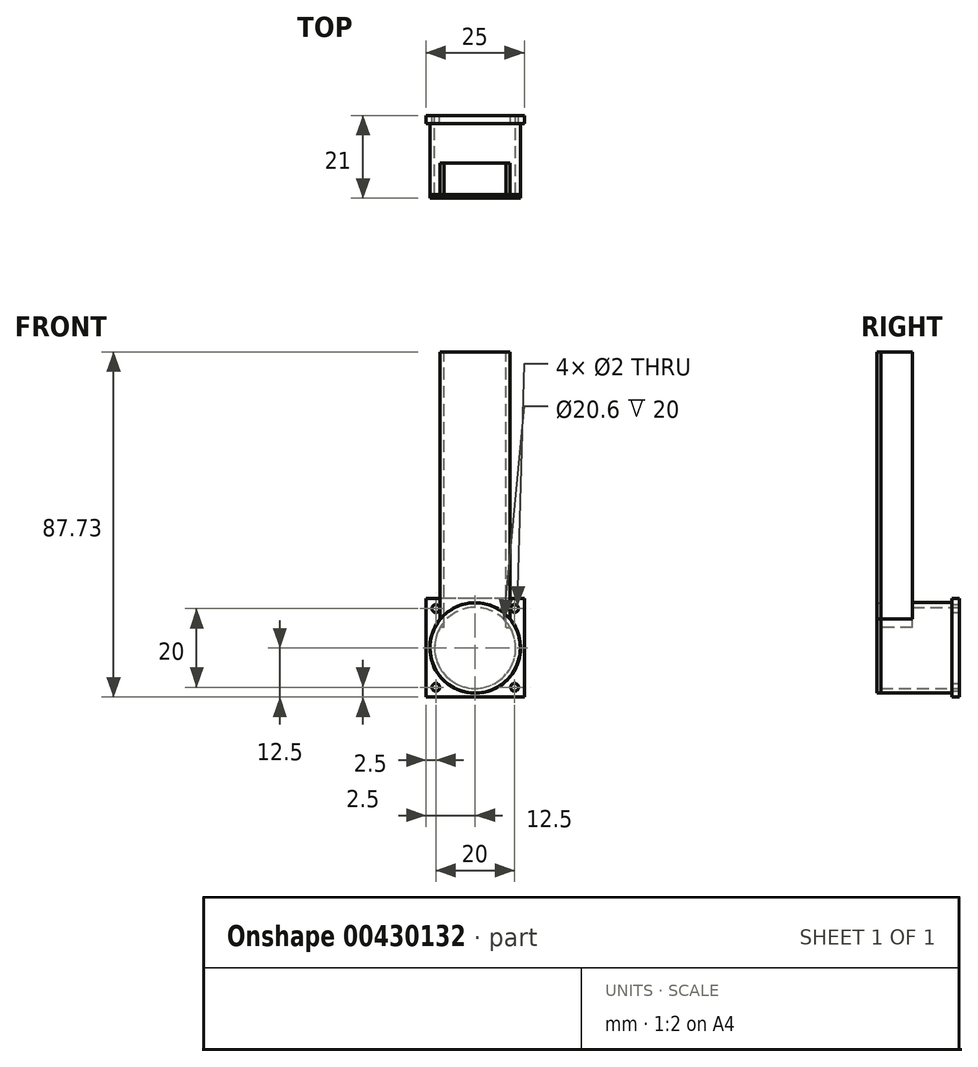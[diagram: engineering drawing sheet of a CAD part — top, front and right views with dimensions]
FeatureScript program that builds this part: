
annotation { "Feature Type Name" : "Feature", "Feature Type Description" : "" }
export const myFeature = defineFeature(function(context is Context, id is Id, definition is map)
    precondition{}
    {
        {
            var Q0;
            Q0=qCreatedBy(makeId("Front.planeOp"),FACE);
            var sketch = newSketch(context, id + "F0", { "sketchPlane" : qUnion([Q0])});
            skLineSegment(sketch, "E0.bottom", {"start": v(12.5, 12.5) * mm, "end": v(-12.5, 12.5) * mm});
            skLineSegment(sketch, "E0.top", {"start": v(12.5, -12.5) * mm, "end": v(-12.5, -12.5) * mm});
            skLineSegment(sketch, "E0.left", {"start": v(12.5, 12.5) * mm, "end": v(12.5, -12.5) * mm});
            skLineSegment(sketch, "E0.right", {"start": v(-12.5, 12.5) * mm, "end": v(-12.5, -12.5) * mm});
            skPoint(sketch, "E0.middle", {"position": v(0, 0) * mm});
            skCircle(sketch, "E1", {"center": v(0, 0) * mm, "radius": 11.5 * mm});
            skCircle(sketch, "E2.0", {"center": v(0, 0) * mm, "radius": 10.3 * mm});
            skCircle(sketch, "E3", {"center": v(-10, 10) * mm, "radius": 1 * mm});
            skLineSegment(sketch, "E4", {"start": v(0, -14.34) * mm, "end": v(0, 50.34) * mm, "construction": true});
            skLineSegment(sketch, "E5", {"start": v(-25.01, 0) * mm, "end": v(43.33, 0) * mm, "construction": true});
            skCircle(sketch, "E6.MirrorC", {"center": v(10, 10) * mm, "radius": 1 * mm});
            skCircle(sketch, "E7.MirrorC", {"center": v(-10, -10) * mm, "radius": 1 * mm});
            skCircle(sketch, "E8.MirrorC", {"center": v(10, -10) * mm, "radius": 1 * mm});
            skLineSegment(sketch, "E9", {"start": v(0, 50.34) * mm, "end": v(0, 167.06) * mm, "construction": true});
            skSolve(sketch);
        }
        {
            var Q0;
            Q0=makeQuery(id+"F0.imprint","IMPRINT",FACE,{"disambiguationData":[TD([[makeQuery(id+"F0.imprint","IMPRINT",EDGE,{"derivedFrom":sQuery(id+"F0.wireOp",EDGE,"E1")}),1.0]])]});
            extrude(context, id + "F1", {"entities" : qUnion([Q0]), "depth" : 20 * mm});
        }
        {
            var Q0;
            Q0 = qSketchRegion(id + "F0", true);
            extrude(context, id + "F2", {"entities" : qUnion([Q0]), "operationType" : NewBodyOperationType.ADD, "depth" : 2 * mm});
        }
        {
            var Q0;
            Q0=makeQuery(id+"F1.opExtrude","CAP_FACE",FACE,{"disambiguationData":[OSD([sQuery(id+"F0.wireOp",EDGE,"E1"),sQuery(id+"F0.wireOp",EDGE,"E2.0")])],"isStart":false});
            var sketch = newSketch(context, id + "F3", { "sketchPlane" : qUnion([Q0])});
            skLineSegment(sketch, "E10", {"start": v(-8.88, 7.31) * mm, "end": v(-8.88, 5.23) * mm});
            skLineSegment(sketch, "E11.MirrorCS", {"start": v(8.88, 7.31) * mm, "end": v(8.88, 5.23) * mm});
            skLineSegment(sketch, "E12", {"start": v(0, 14.57) * mm, "end": v(0, -15.36) * mm, "construction": true});
            skSolve(sketch);
        }
        {
            var Q0;
            Q0 = qSketchRegion(id + "F3", true);
            var Q1;
            {var subQ0=sQuery(id+"F3.wireOp",EDGE,"E10");Q1=makeQuery(id+"F3.imprint","IMPRINT",FACE,{"disambiguationData":[TD([[makeQuery(id+"F3.imprint","IMPRINT",EDGE,{"derivedFrom":subQ0}),1.0]])]});}
            extrude(context, id + "F4", {"entities" : qUnion([Q0, Q1]), "operationType" : NewBodyOperationType.REMOVE, "oppositeDirection" : true, "depth" : 8 * mm});
        }
        {
            var Q0;
            Q0=makeQuery(id+"F1.opExtrude","CAP_FACE",FACE,{"disambiguationData":[OSD([sQuery(id+"F0.wireOp",EDGE,"E1"),sQuery(id+"F0.wireOp",EDGE,"E2.0")])],"isStart":false});
            var sketch = newSketch(context, id + "F5", { "sketchPlane" : qUnion([Q0])});
            skCircle(sketch, "E13", {"center": v(0, 0) * mm, "radius": 11.46 * mm});
            skSolve(sketch);
        }
        {
            var Q0;
            Q0 = qSketchRegion(id + "F5", true);
            extrude(context, id + "F6", {"entities" : qUnion([Q0]), "operationType" : NewBodyOperationType.ADD, "depth" : 1 * mm});
        }
        {
            var Q0;
            Q0=makeQuery(id+"F4.boolean.opBoolean","COPY",FACE,{"derivedFrom":makeQuery(id+"F4.opExtrude","SWEPT_FACE",FACE,{"disambiguationData":[OSD([sQuery(id+"F3.wireOp",EDGE,"E10")])]})});
            var sketch = newSketch(context, id + "F7", { "sketchPlane" : qUnion([Q0])});
            skLineSegment(sketch, "E14", {"start": v(-20, 5.23) * mm, "end": v(-20, 75.23) * mm});
            skLineSegment(sketch, "E15", {"start": v(-12, 5.23) * mm, "end": v(-12, 75.23) * mm});
            skLineSegment(sketch, "E16", {"start": v(-20, 75.23) * mm, "end": v(-12, 75.23) * mm});
            skLineSegment(sketch, "E17", {"start": v(-12, 5.23) * mm, "end": v(-20, 5.23) * mm});
            skSolve(sketch);
        }
        {
            var Q0;
            Q0=makeQuery(id+"F4.boolean.opBoolean","COPY",FACE,{"derivedFrom":makeQuery(id+"F4.opExtrude","SWEPT_FACE",FACE,{"disambiguationData":[OSD([sQuery(id+"F3.wireOp",EDGE,"E11.MirrorCS")])]})});
            var sketch = newSketch(context, id + "F8", { "sketchPlane" : qUnion([Q0])});
            skLineSegment(sketch, "E18", {"start": v(20, 5.23) * mm, "end": v(20, 75.23) * mm});
            skLineSegment(sketch, "E19", {"start": v(12, 5.23) * mm, "end": v(12, 75.23) * mm});
            skLineSegment(sketch, "E20", {"start": v(12, 75.23) * mm, "end": v(20, 75.23) * mm});
            skLineSegment(sketch, "E21", {"start": v(12, 5.23) * mm, "end": v(20, 5.23) * mm});
            skSolve(sketch);
        }
        {
            var Q0;
            Q0 = qSketchRegion(id + "F8", true);
            extrude(context, id + "F9", {"entities" : qUnion([Q0]), "operationType" : NewBodyOperationType.ADD, "depth" : 1 * mm});
        }
        {
            var Q0;
            Q0 = qSketchRegion(id + "F7", true);
            extrude(context, id + "F10", {"entities" : qUnion([Q0]), "operationType" : NewBodyOperationType.ADD, "depth" : 1 * mm});
        }
        {
            var Q0;
            Q0=makeQuery(id+"F10.boolean.opBoolean","MERGE",FACE,{"derivedFrom":[makeQuery(id+"F9.boolean.opBoolean","MERGE",FACE,{"derivedFrom":[makeQuery(id+"F1.opExtrude","CAP_FACE",FACE,{"disambiguationData":[OSD([sQuery(id+"F0.wireOp",EDGE,"E1"),sQuery(id+"F0.wireOp",EDGE,"E2.0")])],"isStart":false}),makeQuery(id+"F9.opExtrude","SWEPT_FACE",FACE,{"disambiguationData":[OSD([sQuery(id+"F8.wireOp",EDGE,"E18")])]})]}),makeQuery(id+"F10.opExtrude","SWEPT_FACE",FACE,{"disambiguationData":[OSD([sQuery(id+"F7.wireOp",EDGE,"E14")])]})]});
            var sketch = newSketch(context, id + "F11", { "sketchPlane" : qUnion([Q0])});
            skLineSegment(sketch, "E22", {"start": v(-8.88, 75.23) * mm, "end": v(8.87, 75.23) * mm});
            skArc(sketch, "E23", {"start": v(8.88, 7.31) * mm, "mid": v(0, 11.46) * mm, "end": v(-8.88, 7.31) * mm});
            skLineSegment(sketch, "E24", {"start": v(-8.88, 7.31) * mm, "end": v(-8.88, 75.23) * mm});
            skLineSegment(sketch, "E25", {"start": v(8.87, 75.23) * mm, "end": v(8.88, 7.31) * mm});
            skSolve(sketch);
        }
        {
            var Q0;
            Q0 = qSketchRegion(id + "F11", true);
            extrude(context, id + "F12", {"entities" : qUnion([Q0]), "depth" : 1 * mm});
        }
    });
